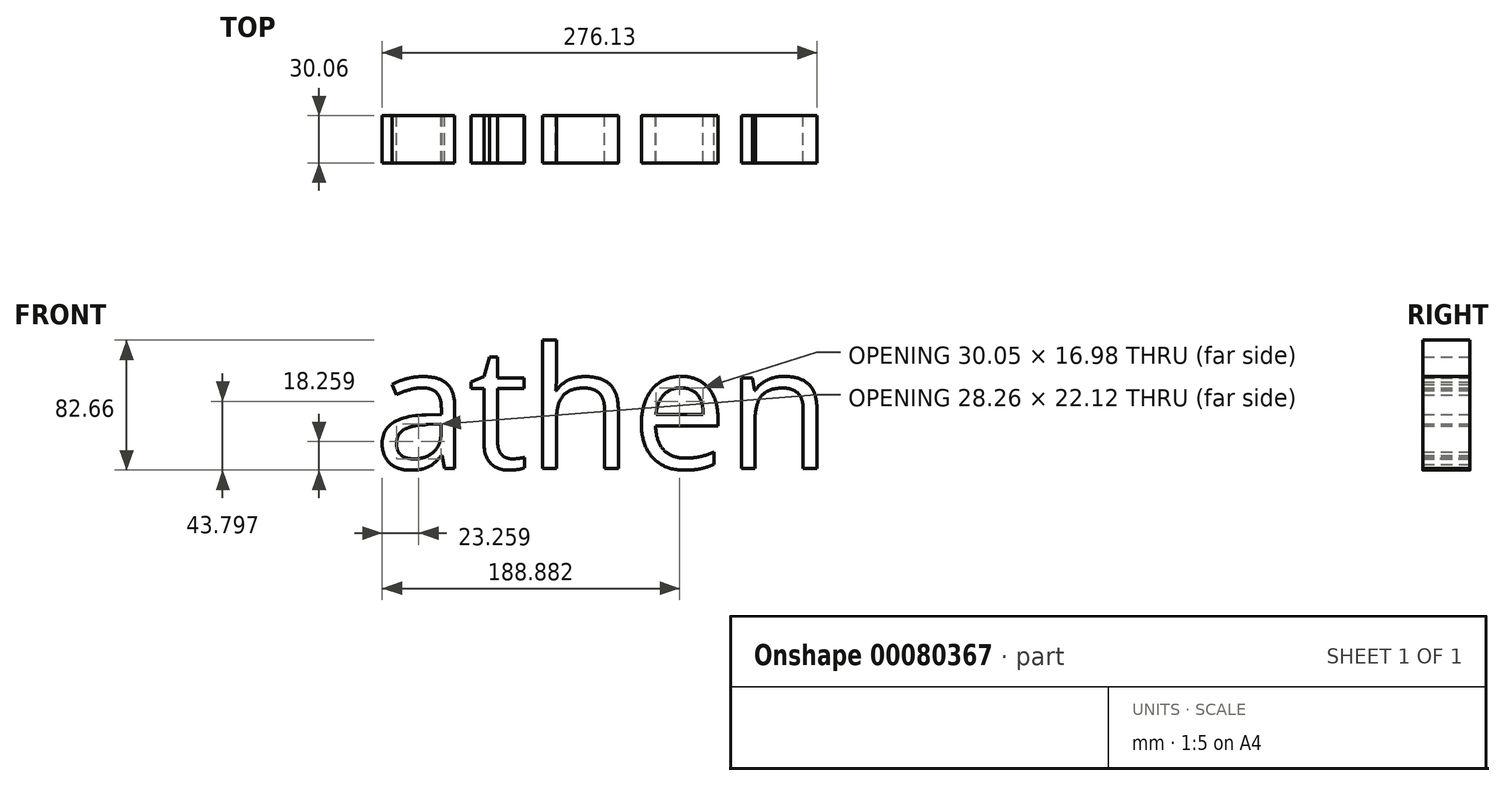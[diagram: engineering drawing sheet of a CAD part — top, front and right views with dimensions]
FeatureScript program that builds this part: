
annotation { "Feature Type Name" : "Feature", "Feature Type Description" : "" }
export const myFeature = defineFeature(function(context is Context, id is Id, definition is map)
    precondition{}
    {
        {
            var Q0;
            Q0=qCreatedBy(makeId("Front.planeOp"),FACE);
            var sketch = newSketch(context, id + "F0", { "sketchPlane" : qUnion([Q0])});
            skText(sketch, "E0", { "text": "athen", "fontName": "OpenSans-Regular.ttf"});
            const initialGuessF0  = {"E0": [-0.01827, -0.04838, 1, 0, 0.07732]};
            skSetInitialGuess(sketch, initialGuessF0);
            skSolve(sketch);
        }
        {
            var Q0;
            Q0 = qSketchRegion(id + "F0", true);
            extrude(context, id + "F1", {"entities" : qUnion([Q0]), "depth" : 30.06 * mm});
        }
    });
